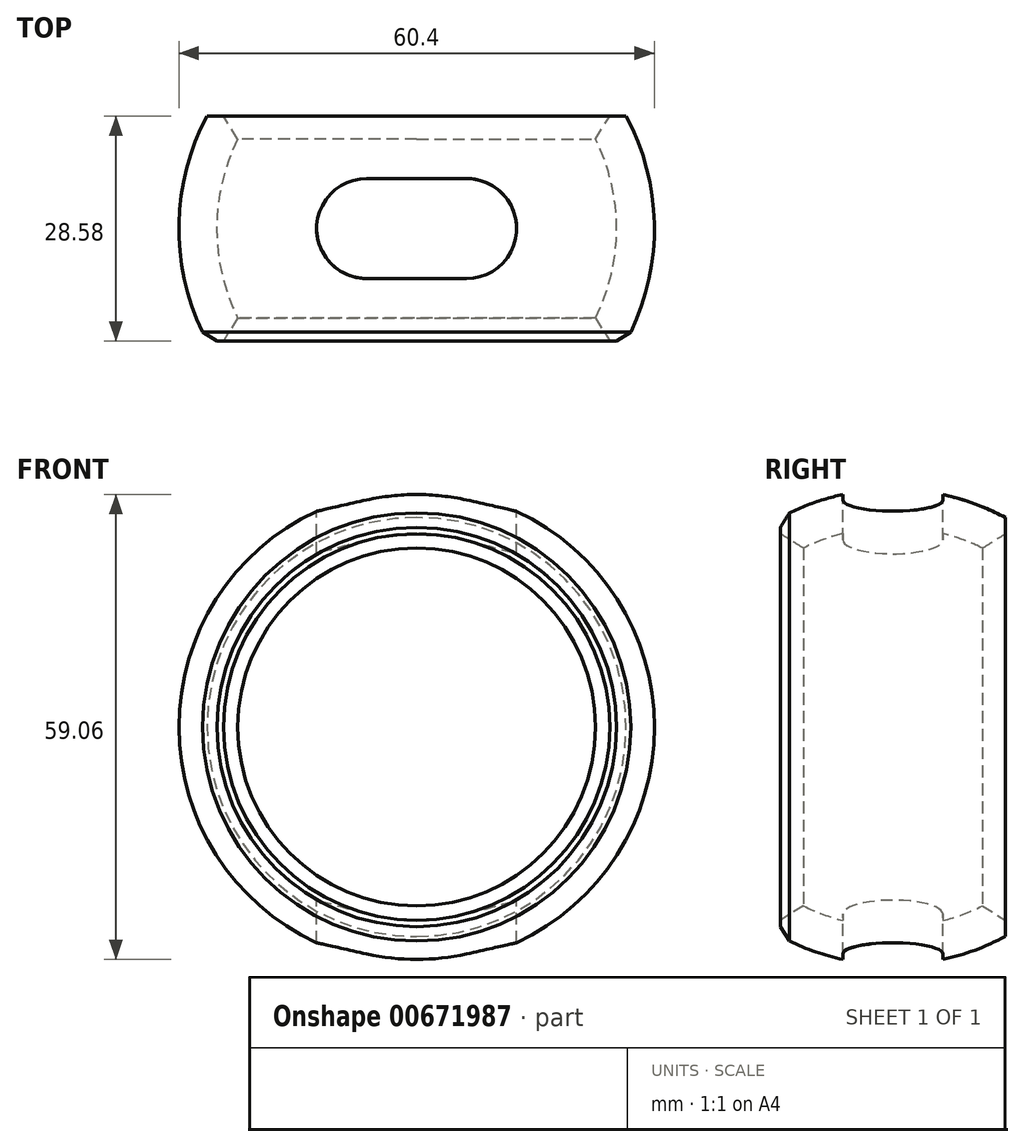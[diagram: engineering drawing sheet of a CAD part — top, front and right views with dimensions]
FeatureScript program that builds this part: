
annotation { "Feature Type Name" : "Feature", "Feature Type Description" : "" }
export const myFeature = defineFeature(function(context is Context, id is Id, definition is map)
    precondition{}
    {
        {
            var Q0;
            Q0=qCreatedBy(makeId("Top.planeOp"),FACE);
            var sketch = newSketch(context, id + "F0", { "sketchPlane" : qUnion([Q0])});
            skArc(sketch, "E0", {"start": v(21, -14.29) * mm, "mid": v(25.4, 0) * mm, "end": v(21, 14.29) * mm});
            skLineSegment(sketch, "E1.bottom", {"start": v(26.61, -14.29) * mm, "end": v(21, -14.29) * mm});
            skLineSegment(sketch, "E1.top", {"start": v(26.61, 14.29) * mm, "end": v(21, 14.29) * mm});
            skPoint(sketch, "E2.bottom.end.orphan", {"position": v(-7.96, 52.56) * mm});
            skPoint(sketch, "E2.bottom.start.orphan", {"position": v(7.96, 52.56) * mm});
            skPoint(sketch, "E1.right.end.orphan", {"position": v(-53.12, 14.29) * mm});
            skPoint(sketch, "E3.orphan", {"position": v(-53.12, -14.29) * mm});
            skArc(sketch, "E4.trimOffspring", {"start": v(26.61, -14.29) * mm, "mid": v(30.2, 0) * mm, "end": v(26.61, 14.29) * mm});
            skPoint(sketch, "E2.top.end.orphan", {"position": v(-7.96, -52.56) * mm});
            skPoint(sketch, "E2.top.start.orphan", {"position": v(7.96, -52.56) * mm});
            skPoint(sketch, "E5.orphan", {"position": v(53.12, 14.29) * mm});
            skPoint(sketch, "E6.orphan", {"position": v(53.12, -14.29) * mm});
            skLineSegment(sketch, "E7", {"start": v(0, -4.03) * mm, "end": v(0, 5.15) * mm});
            skSolve(sketch);
        }
        {
            var Q0;
            Q0=makeQuery(id+"F0.imprint","IMPRINT",FACE,{"disambiguationData":[TD([[makeQuery(id+"F0.imprint","IMPRINT",EDGE,{"derivedFrom":sQuery(id+"F0.wireOp",EDGE,"E0")}),-1.0]])]});
            var Q1;
            Q1=sQuery(id+"F0.wireOp",EDGE,"E7");
            revolve(context, id + "F1", {"entities" : qUnion([Q0]), "axis" : qUnion([Q1]), "revolveType" : RevolveType.FULL});
        }
        {
            var Q0;
            Q0=makeQuery(id+"F1.opRevolve","SWEPT_EDGE",EDGE,{"disambiguationData":[OSD([sQuery(id+"F0.wireOp",EDGE,"E0"),sQuery(id+"F0.wireOp",EDGE,"E1.top")])]});
            chamfer(context, id + "F2", {"entities" : qUnion([Q0]), "width" : 2.03 * mm, "tangentPropagation" : true});
        }
        {
            var Q0;
            Q0=qCreatedBy(makeId("Top.planeOp"),FACE);
            var sketch = newSketch(context, id + "F3", { "sketchPlane" : qUnion([Q0])});
            skLineSegment(sketch, "E8.bottom", {"start": v(6.35, -6.35) * mm, "end": v(-6.35, -6.35) * mm});
            skLineSegment(sketch, "E8.top", {"start": v(6.35, 6.35) * mm, "end": v(-6.35, 6.35) * mm});
            skLineSegment(sketch, "E8.left", {"start": v(12.7, 0) * mm, "end": v(12.7, 0) * mm});
            skLineSegment(sketch, "E8.right", {"start": v(-12.7, 0) * mm, "end": v(-12.7, 0) * mm});
            skPoint(sketch, "E8.middle", {"position": v(0, 0) * mm});
            skPoint(sketch, "E9.visualSharp", {"position": v(12.7, 6.35) * mm});
            skArc(sketch, "E9.filletArc", {"start": v(12.7, 0) * mm, "mid": v(10.84, 4.5) * mm, "end": v(6.35, 6.35) * mm});
            skPoint(sketch, "E10.visualSharp", {"position": v(12.7, -6.35) * mm});
            skArc(sketch, "E10.filletArc", {"start": v(6.35, -6.35) * mm, "mid": v(10.84, -4.5) * mm, "end": v(12.7, 0) * mm});
            skPoint(sketch, "E11.visualSharp", {"position": v(-12.7, -6.35) * mm});
            skArc(sketch, "E11.filletArc", {"start": v(-12.7, 0) * mm, "mid": v(-10.84, -4.5) * mm, "end": v(-6.35, -6.35) * mm});
            skPoint(sketch, "E12.visualSharp", {"position": v(-12.7, 6.35) * mm});
            skArc(sketch, "E12.filletArc", {"start": v(-6.35, 6.35) * mm, "mid": v(-10.84, 4.5) * mm, "end": v(-12.7, 0) * mm});
            skSolve(sketch);
        }
        {
            var Q0;
            Q0=makeQuery(id+"F1.opRevolve","SWEPT_FACE",FACE,{"disambiguationData":[OSD([sQuery(id+"F0.wireOp",EDGE,"E1.bottom")])]});
            chamfer(context, id + "F4", {"entities" : qUnion([Q0]), "width" : 2.03 * mm, "tangentPropagation" : true});
        }
        {
            var Q0;
            Q0 = qSketchRegion(id + "F3", true);
            extrude(context, id + "F5", {"entities" : qUnion([Q0]), "operationType" : NewBodyOperationType.ADD, "endBound" : BoundingType.SYMMETRIC, "depth" : 76.2 * mm, "offsetDistance" : 25.4 * mm});
        }
        {
            var Q0;
            Q0=makeQuery(id+"F5.opExtrude","CAP_FACE",FACE,{"disambiguationData":[OSD([sQuery(id+"F3.wireOp",EDGE,"E8.bottom"),sQuery(id+"F3.wireOp",EDGE,"E8.top"),sQuery(id+"F3.wireOp",EDGE,"E9.filletArc"),sQuery(id+"F3.wireOp",EDGE,"E10.filletArc"),sQuery(id+"F3.wireOp",EDGE,"E11.filletArc"),sQuery(id+"F3.wireOp",EDGE,"E12.filletArc")])],"isStart":false});
            extrude(context, id + "F6", {"entities" : qUnion([Q0]), "operationType" : NewBodyOperationType.REMOVE, "endBound" : BoundingType.SYMMETRIC, "oppositeDirection" : true, "depth" : 584.2 * mm, "offsetDistance" : 25.4 * mm});
        }
        {
            var Q0;
            Q0=qCreatedBy(makeId("Front.planeOp"),FACE);
            var sketch = newSketch(context, id + "F7", { "sketchPlane" : qUnion([Q0])});
            skLineSegment(sketch, "E13", {"start": v(0, 0) * mm, "end": v(31.95, -18.45) * mm});
            skLineSegment(sketch, "E14", {"start": v(0, 0) * mm, "end": v(36.13, 20.86) * mm});
            skSolve(sketch);
        }
    });
